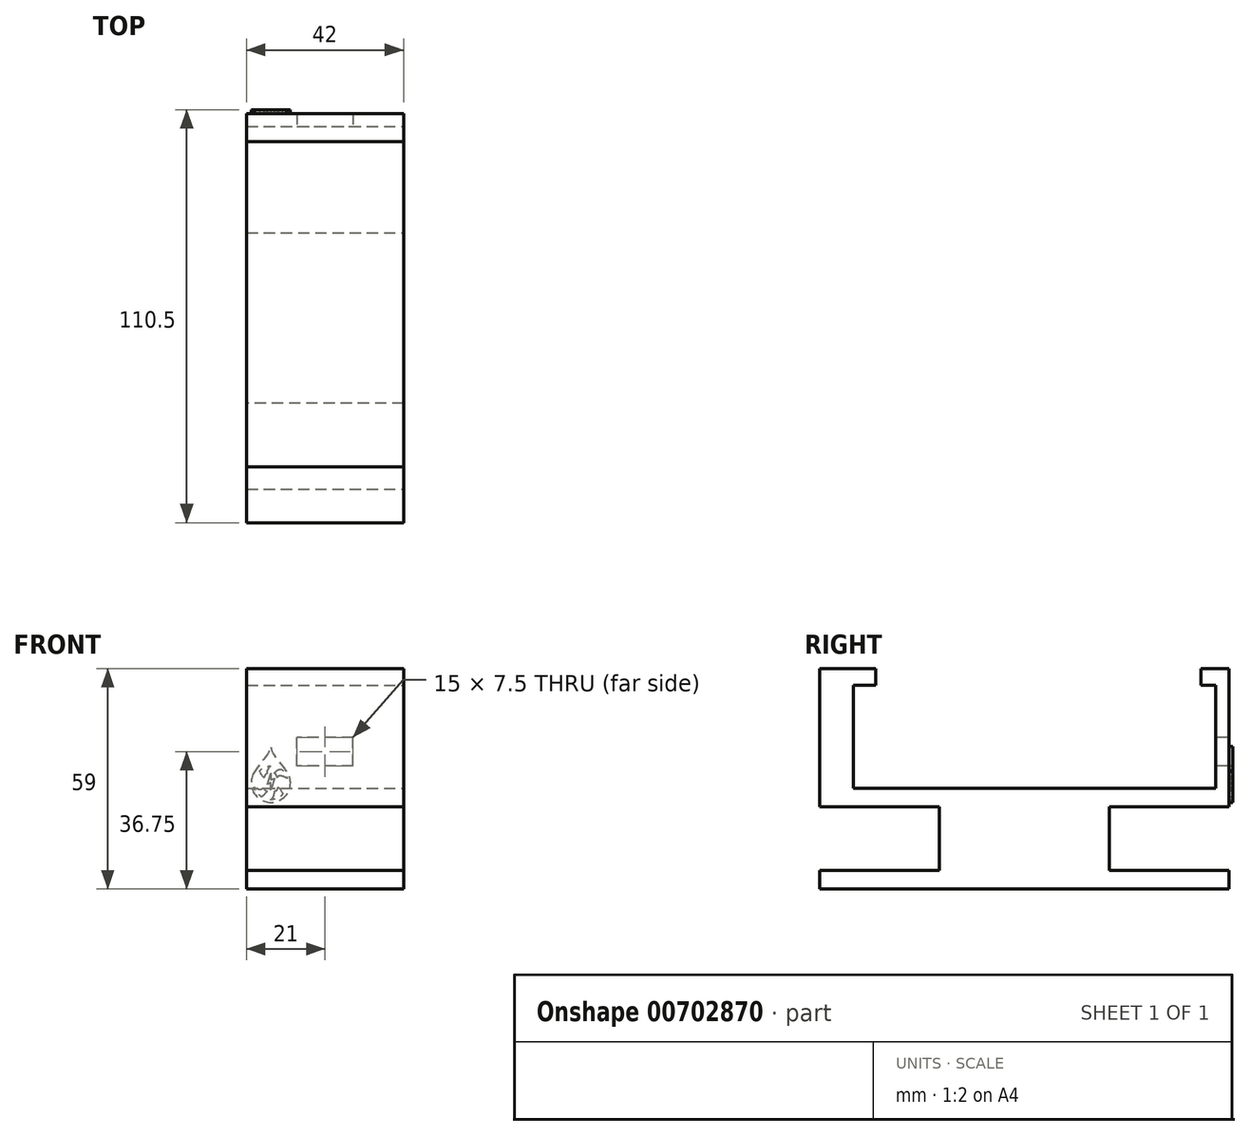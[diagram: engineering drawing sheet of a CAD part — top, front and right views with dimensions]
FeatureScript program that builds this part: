
annotation { "Feature Type Name" : "Feature", "Feature Type Description" : "" }
export const myFeature = defineFeature(function(context is Context, id is Id, definition is map)
    precondition{}
    {
        {
            var Q0;
            Q0=qCreatedBy(makeId("Top.planeOp"),FACE);
            var sketch = newSketch(context, id + "F0", { "sketchPlane" : qUnion([Q0])});
            skLineSegment(sketch, "E0.bottom", {"start": v(-21, 54.75) * mm, "end": v(21, 54.75) * mm});
            skLineSegment(sketch, "E0.top", {"start": v(-21, -54.75) * mm, "end": v(21, -54.75) * mm});
            skLineSegment(sketch, "E0.left", {"start": v(-21, 54.75) * mm, "end": v(-21, -54.75) * mm});
            skLineSegment(sketch, "E0.right", {"start": v(21, 54.75) * mm, "end": v(21, -54.75) * mm});
            skPoint(sketch, "E0.middle", {"position": v(0, 0) * mm});
            skSolve(sketch);
        }
        {
            var Q0;
            Q0=makeQuery(id+"F0.imprint","IMPRINT",FACE,{"disambiguationData":[TD([[makeQuery(id+"F0.imprint","IMPRINT",EDGE,{"derivedFrom":sQuery(id+"F0.wireOp",EDGE,"E0.bottom")}),-1.0]])]});
            extrude(context, id + "F1", {"entities" : qUnion([Q0]), "depth" : 5 * mm, "offsetDistance" : 25 * mm});
        }
        {
            var Q0;
            Q0=makeQuery(id+"F1.opExtrude","CAP_FACE",FACE,{"disambiguationData":[OSD([sQuery(id+"F0.wireOp",EDGE,"E0.bottom"),sQuery(id+"F0.wireOp",EDGE,"E0.top"),sQuery(id+"F0.wireOp",EDGE,"E0.left"),sQuery(id+"F0.wireOp",EDGE,"E0.right")])],"isStart":false});
            var sketch = newSketch(context, id + "F2", { "sketchPlane" : qUnion([Q0])});
            skLineSegment(sketch, "E1.bottom", {"start": v(-21, 54.75) * mm, "end": v(21, 54.75) * mm});
            skLineSegment(sketch, "E1.top", {"start": v(-21, 47.25) * mm, "end": v(21, 47.25) * mm});
            skLineSegment(sketch, "E1.left", {"start": v(-21, 54.75) * mm, "end": v(-21, 47.25) * mm});
            skLineSegment(sketch, "E1.right", {"start": v(21, 54.75) * mm, "end": v(21, 47.25) * mm});
            skPoint(sketch, "E1.middle", {"position": v(0, 51) * mm});
            skLineSegment(sketch, "E2.bottom", {"start": v(-21, -39.75) * mm, "end": v(21, -39.75) * mm});
            skLineSegment(sketch, "E2.top", {"start": v(-21, -54.75) * mm, "end": v(21, -54.75) * mm});
            skLineSegment(sketch, "E2.left", {"start": v(-21, -39.75) * mm, "end": v(-21, -54.75) * mm});
            skLineSegment(sketch, "E2.right", {"start": v(21, -39.75) * mm, "end": v(21, -54.75) * mm});
            skPoint(sketch, "E2.middle", {"position": v(0, -47.25) * mm});
            skSolve(sketch);
        }
        {
            var Q0;
            Q0=makeQuery(id+"F2.imprint","IMPRINT",FACE,{"disambiguationData":[TD([[makeQuery(id+"F2.imprint","IMPRINT",EDGE,{"derivedFrom":sQuery(id+"F2.wireOp",EDGE,"gTRGSuqZ-lPxv-xSsv-gjWA-rCe4dbmy2frY.bottom")}),-1.0]])]});
            var Q1;
            Q1=makeQuery(id+"F2.imprint","IMPRINT",FACE,{"disambiguationData":[TD([[makeQuery(id+"F2.imprint","IMPRINT",EDGE,{"derivedFrom":sQuery(id+"F2.wireOp",EDGE,"5NfKlNX9-xNwy-tjNF-5iGd-XRvzVmTsgCSR.bottom")}),1.0]])]});
            var Q2;
            Q2=makeQuery(id+"F2.imprint","IMPRINT",FACE,{"disambiguationData":[TD([[makeQuery(id+"F2.imprint","IMPRINT",EDGE,{"derivedFrom":sQuery(id+"F2.wireOp",EDGE,"E1.bottom")}),-1.0]])]});
            var Q3;
            Q3=makeQuery(id+"F2.imprint","IMPRINT",FACE,{"disambiguationData":[TD([[makeQuery(id+"F2.imprint","IMPRINT",EDGE,{"derivedFrom":sQuery(id+"F2.wireOp",EDGE,"E2.bottom")}),-1.0]])]});
            extrude(context, id + "F3", {"entities" : qUnion([Q0, Q1, Q2, Q3]), "operationType" : NewBodyOperationType.ADD, "depth" : 32 * mm, "offsetDistance" : 25 * mm});
        }
        {
            var Q0;
            Q0=makeQuery(id+"F3.opExtrude","SWEPT_FACE",FACE,{"disambiguationData":[OSD([sQuery(id+"F2.wireOp",EDGE,"E1.top")])]});
            var sketch = newSketch(context, id + "F4", { "sketchPlane" : qUnion([Q0])});
            skLineSegment(sketch, "E3.bottom", {"start": v(-21, 32.5) * mm, "end": v(21, 32.5) * mm});
            skLineSegment(sketch, "E3.top", {"start": v(-21, 5) * mm, "end": v(21, 5) * mm});
            skLineSegment(sketch, "E3.left", {"start": v(-21, 32.5) * mm, "end": v(-21, 5) * mm});
            skLineSegment(sketch, "E3.right", {"start": v(21, 32.5) * mm, "end": v(21, 5) * mm});
            skSolve(sketch);
        }
        {
            var Q0;
            Q0=makeQuery(id+"F4.imprint","IMPRINT",FACE,{"disambiguationData":[TD([[makeQuery(id+"F4.imprint","IMPRINT",EDGE,{"derivedFrom":sQuery(id+"F4.wireOp",EDGE,"E3.bottom")}),-1.0]])]});
            extrude(context, id + "F5", {"entities" : qUnion([Q0]), "operationType" : NewBodyOperationType.REMOVE, "oppositeDirection" : true, "depth" : 4 * mm, "offsetDistance" : 25 * mm});
        }
        {
            var Q0;
            Q0=makeQuery(id+"F3.opExtrude","SWEPT_FACE",FACE,{"disambiguationData":[OSD([sQuery(id+"F2.wireOp",EDGE,"E2.bottom")])]});
            var sketch = newSketch(context, id + "F6", { "sketchPlane" : qUnion([Q0])});
            skLineSegment(sketch, "E4.bottom", {"start": v(-21, 32.5) * mm, "end": v(21, 32.5) * mm});
            skLineSegment(sketch, "E4.top", {"start": v(-21, 5) * mm, "end": v(21, 5) * mm});
            skLineSegment(sketch, "E4.left", {"start": v(-21, 32.5) * mm, "end": v(-21, 5) * mm});
            skLineSegment(sketch, "E4.right", {"start": v(21, 32.5) * mm, "end": v(21, 5) * mm});
            skSolve(sketch);
        }
        {
            var Q0;
            Q0=makeQuery(id+"F6.imprint","IMPRINT",FACE,{"disambiguationData":[TD([[makeQuery(id+"F6.imprint","IMPRINT",EDGE,{"derivedFrom":sQuery(id+"F6.wireOp",EDGE,"E4.bottom")}),-1.0]])]});
            extrude(context, id + "F7", {"entities" : qUnion([Q0]), "operationType" : NewBodyOperationType.REMOVE, "oppositeDirection" : true, "depth" : 6 * mm, "offsetDistance" : 25 * mm});
        }
        {
            var Q0;
            Q0=makeQuery(id+"F5.boolean.opBoolean","COPY",FACE,{"derivedFrom":makeQuery(id+"F5.opExtrude","CAP_FACE",FACE,{"disambiguationData":[OSD([sQuery(id+"F4.wireOp",EDGE,"E3.bottom"),sQuery(id+"F4.wireOp",EDGE,"E3.top"),sQuery(id+"F4.wireOp",EDGE,"E3.left"),sQuery(id+"F4.wireOp",EDGE,"E3.right")])],"isStart":false})});
            var sketch = newSketch(context, id + "F8", { "sketchPlane" : qUnion([Q0])});
            skLineSegment(sketch, "E5.bottom", {"start": v(-7.5, 18.5) * mm, "end": v(7.5, 18.5) * mm});
            skLineSegment(sketch, "E5.top", {"start": v(-7.5, 11) * mm, "end": v(7.5, 11) * mm});
            skLineSegment(sketch, "E5.left", {"start": v(-7.5, 18.5) * mm, "end": v(-7.5, 11) * mm});
            skLineSegment(sketch, "E5.right", {"start": v(7.5, 18.5) * mm, "end": v(7.5, 11) * mm});
            skPoint(sketch, "E5.middle", {"position": v(0, 14.75) * mm});
            skSolve(sketch);
        }
        {
            var Q0;
            Q0=makeQuery(id+"F8.imprint","IMPRINT",FACE,{"disambiguationData":[TD([[makeQuery(id+"F8.imprint","IMPRINT",EDGE,{"derivedFrom":sQuery(id+"F8.wireOp",EDGE,"E5.bottom")}),-1.0]])]});
            extrude(context, id + "F9", {"entities" : qUnion([Q0]), "operationType" : NewBodyOperationType.REMOVE, "endBound" : BoundingType.THROUGH_ALL, "oppositeDirection" : true, "depth" : 25 * mm, "offsetDistance" : 25 * mm});
        }
        {
            var Q0;
            Q0=makeQuery(id+"F1.opExtrude","CAP_FACE",FACE,{"disambiguationData":[OSD([sQuery(id+"F0.wireOp",EDGE,"E0.bottom"),sQuery(id+"F0.wireOp",EDGE,"E0.top"),sQuery(id+"F0.wireOp",EDGE,"E0.left"),sQuery(id+"F0.wireOp",EDGE,"E0.right")])],"isStart":true});
            var sketch = newSketch(context, id + "F10", { "sketchPlane" : qUnion([Q0])});
            skLineSegment(sketch, "E6.bottom", {"start": v(-21, -54.75) * mm, "end": v(21, -54.75) * mm});
            skLineSegment(sketch, "E6.top", {"start": v(-21, 0) * mm, "end": v(21, 0) * mm});
            skLineSegment(sketch, "E6.left", {"start": v(-21, -54.75) * mm, "end": v(-21, 0) * mm});
            skLineSegment(sketch, "E6.right", {"start": v(21, -54.75) * mm, "end": v(21, 0) * mm});
            skLineSegment(sketch, "E7.bottom", {"start": v(-21, 54.75) * mm, "end": v(21, 54.75) * mm});
            skLineSegment(sketch, "E7.left", {"start": v(-21, 54.75) * mm, "end": v(-21, 0) * mm});
            skLineSegment(sketch, "E7.right", {"start": v(21, 54.75) * mm, "end": v(21, 0) * mm});
            skSolve(sketch);
        }
        {
            var Q0;
            Q0 = qSketchRegion(id + "F10", true);
            extrude(context, id + "F11", {"entities" : qUnion([Q0]), "operationType" : NewBodyOperationType.ADD, "depth" : 22 * mm, "offsetDistance" : 25 * mm});
        }
        {
            var Q0;
            Q0=makeQuery(id+"F11.boolean.opBoolean","MERGE",FACE,{"derivedFrom":[makeQuery(id+"F3.boolean.opBoolean","MERGE",FACE,{"derivedFrom":[makeQuery(id+"F1.opExtrude","SWEPT_FACE",FACE,{"disambiguationData":[OSD([sQuery(id+"F0.wireOp",EDGE,"E0.bottom")])]}),makeQuery(id+"F3.opExtrude","SWEPT_FACE",FACE,{"disambiguationData":[OSD([sQuery(id+"F2.wireOp",EDGE,"E1.bottom")])]})]}),makeQuery(id+"F11.opExtrude","SWEPT_FACE",FACE,{"disambiguationData":[OSD([sQuery(id+"F10.wireOp",EDGE,"E6.bottom")])]})]});
            var sketch = newSketch(context, id + "F12", { "sketchPlane" : qUnion([Q0])});
            skLineSegment(sketch, "E8.bottom", {"start": v(21, -17) * mm, "end": v(-21, -17) * mm});
            skLineSegment(sketch, "E8.top", {"start": v(21, 0) * mm, "end": v(-21, 0) * mm});
            skLineSegment(sketch, "E8.left", {"start": v(21, -17) * mm, "end": v(21, 0) * mm});
            skLineSegment(sketch, "E8.right", {"start": v(-21, -17) * mm, "end": v(-21, 0) * mm});
            skSolve(sketch);
        }
        {
            var Q0;
            Q0=makeQuery(id+"F12.imprint","IMPRINT",FACE,{"disambiguationData":[TD([[makeQuery(id+"F12.imprint","IMPRINT",EDGE,{"derivedFrom":sQuery(id+"F12.wireOp",EDGE,"E8.bottom")}),-1.0]])]});
            extrude(context, id + "F13", {"entities" : qUnion([Q0]), "operationType" : NewBodyOperationType.REMOVE, "oppositeDirection" : true, "depth" : 32 * mm, "offsetDistance" : 25 * mm});
        }
        {
            var Q0;
            Q0=makeQuery(id+"F11.boolean.opBoolean","MERGE",FACE,{"derivedFrom":[makeQuery(id+"F3.boolean.opBoolean","MERGE",FACE,{"derivedFrom":[makeQuery(id+"F1.opExtrude","SWEPT_FACE",FACE,{"disambiguationData":[OSD([sQuery(id+"F0.wireOp",EDGE,"E0.top")])]}),makeQuery(id+"F3.opExtrude","SWEPT_FACE",FACE,{"disambiguationData":[OSD([sQuery(id+"F2.wireOp",EDGE,"E2.top")])]})]}),makeQuery(id+"F11.opExtrude","SWEPT_FACE",FACE,{"disambiguationData":[OSD([sQuery(id+"F10.wireOp",EDGE,"E7.bottom")])]})]});
            var sketch = newSketch(context, id + "F14", { "sketchPlane" : qUnion([Q0])});
            skLineSegment(sketch, "E9.bottom", {"start": v(21, -17) * mm, "end": v(-21, -17) * mm});
            skLineSegment(sketch, "E9.top", {"start": v(21, 0) * mm, "end": v(-21, 0) * mm});
            skLineSegment(sketch, "E9.left", {"start": v(21, -17) * mm, "end": v(21, 0) * mm});
            skLineSegment(sketch, "E9.right", {"start": v(-21, -17) * mm, "end": v(-21, 0) * mm});
            skSolve(sketch);
        }
        {
            var Q0;
            Q0=makeQuery(id+"F14.imprint","IMPRINT",FACE,{"disambiguationData":[TD([[makeQuery(id+"F14.imprint","IMPRINT",EDGE,{"derivedFrom":sQuery(id+"F14.wireOp",EDGE,"E9.bottom")}),-1.0]])]});
            extrude(context, id + "F15", {"entities" : qUnion([Q0]), "operationType" : NewBodyOperationType.REMOVE, "oppositeDirection" : true, "depth" : 32 * mm, "offsetDistance" : 25 * mm});
        }
        {
            var Q0;
            {var subQ2=sQuery(id+"F2.wireOp",EDGE,"E1.bottom");Q0=makeQuery(id+"F13.boolean.opBoolean","SPLIT",FACE,{"disambiguationData":[TD([makeQuery(id+"F9.boolean.opBoolean","COPY",FACE,{"derivedFrom":makeQuery(id+"F9.opExtrude","SWEPT_FACE",FACE,{"disambiguationData":[OSD([sQuery(id+"F8.wireOp",EDGE,"E5.bottom")])]})})])],"derivedFrom":makeQuery(id+"F11.boolean.opBoolean","MERGE",FACE,{"derivedFrom":[makeQuery(id+"F3.boolean.opBoolean","MERGE",FACE,{"derivedFrom":[makeQuery(id+"F1.opExtrude","SWEPT_FACE",FACE,{"disambiguationData":[OSD([sQuery(id+"F0.wireOp",EDGE,"E0.bottom")])]}),makeQuery(id+"F3.opExtrude","SWEPT_FACE",FACE,{"disambiguationData":[OSD([subQ2])]})]}),makeQuery(id+"F11.opExtrude","SWEPT_FACE",FACE,{"disambiguationData":[OSD([sQuery(id+"F10.wireOp",EDGE,"E6.bottom")])]})]})});}
            var sketch = newSketch(context, id + "F16", { "sketchPlane" : qUnion([Q0])});
            skCircle(sketch, "E10", {"center": v(14.5, 6.44) * mm, "radius": 5.26 * mm});
            skFitSpline(sketch, "E11", {"points": [v(9.9, 9) * mm, v(13.99, 14.6) * mm, v(14.56, 16.18) * mm, v(15.14, 14.6) * mm, v(18.8, 9.46) * mm], "startDerivative": vector(16.98, 26.88) * mm, "endDerivative": vector(16.85, -27.07) * mm});
            skLineSegment(sketch, "E12", {"start": v(14.5, 7.28) * mm, "end": v(13.47, 7.64) * mm});
            skLineSegment(sketch, "E13", {"start": v(13.47, 7.64) * mm, "end": v(14.5, 4.52) * mm});
            skLineSegment(sketch, "E14", {"start": v(14.5, 4.52) * mm, "end": v(14.5, 6.44) * mm});
            skLineSegment(sketch, "E15", {"start": v(14.5, 6.44) * mm, "end": v(15.39, 6) * mm});
            skLineSegment(sketch, "E16", {"start": v(15.39, 6) * mm, "end": v(14.5, 9.02) * mm});
            skLineSegment(sketch, "E17", {"start": v(14.5, 9.02) * mm, "end": v(14.5, 7.28) * mm});
            skFitSpline(sketch, "E18", {"points": [v(16.34, 7.72) * mm, v(17.24, 9.89) * mm, v(14.5, 10.94) * mm], "startDerivative": vector(5.76, 7.92) * mm, "endDerivative": vector(-5.08, -0.17) * mm});
            skFitSpline(sketch, "E19", {"points": [v(14.5, 10.94) * mm, v(15.4, 9.02) * mm], "startDerivative": vector(2.42, -1.84) * mm, "endDerivative": vector(-1.27, -0.47) * mm});
            skFitSpline(sketch, "E20", {"points": [v(13.59, 9.02) * mm, v(11.74, 10.05) * mm, v(10.1, 7.6) * mm], "startDerivative": vector(-3.42, 3.64) * mm, "endDerivative": vector(-2.44, -5.45) * mm});
            skFitSpline(sketch, "E21", {"points": [v(10.1, 7.6) * mm, v(12.74, 7.6) * mm], "startDerivative": vector(2.22, 1.16) * mm, "endDerivative": vector(0, -4.31) * mm});
            skFitSpline(sketch, "E22", {"points": [v(15.4, 9.02) * mm, v(16.34, 7.72) * mm], "startDerivative": vector(1.63, -0.68) * mm, "endDerivative": vector(0.65, -1.86) * mm});
            skFitSpline(sketch, "E23", {"points": [v(12.73, 7.73) * mm, v(13.59, 9.02) * mm], "startDerivative": vector(0.63, 2.17) * mm, "endDerivative": vector(1.3, 0.45) * mm});
            skFitSpline(sketch, "E24", {"points": [v(12.51, 5.25) * mm, v(11.53, 3.12) * mm, v(14.56, 1.84) * mm], "startDerivative": vector(-6.57, -6.68) * mm, "endDerivative": vector(5.86, -1.17) * mm});
            skFitSpline(sketch, "E25", {"points": [v(14.56, 1.84) * mm, v(13.57, 4.24) * mm], "startDerivative": vector(-0.1, 0.44) * mm, "endDerivative": vector(0.66, 4.7) * mm});
            skFitSpline(sketch, "E26", {"points": [v(13.57, 4.24) * mm, v(12.51, 5.25) * mm], "startDerivative": vector(-2.26, 0.13) * mm, "endDerivative": vector(-0.52, 1.5) * mm});
            skFitSpline(sketch, "E27", {"points": [v(15.42, 4.18) * mm, v(17.1, 2.77) * mm, v(19.04, 5.25) * mm], "startDerivative": vector(7.14, -6.76) * mm, "endDerivative": vector(2.64, 5.36) * mm});
            skFitSpline(sketch, "E28", {"points": [v(19.04, 5.25) * mm, v(16.47, 5.14) * mm], "startDerivative": vector(-2.16, -0.83) * mm, "endDerivative": vector(-2.61, 2.84) * mm});
            skFitSpline(sketch, "E29", {"points": [v(16.47, 5.14) * mm, v(15.42, 4.18) * mm], "startDerivative": vector(-0.71, -2.15) * mm, "endDerivative": vector(-1.3, -0.4) * mm});
            skSolve(sketch);
        }
        {
            var Q0;
            Q0 = qSketchRegion(id + "F16", true);
            extrude(context, id + "F17", {"entities" : qUnion([Q0]), "operationType" : NewBodyOperationType.ADD, "depth" : 1 * mm, "offsetDistance" : 25 * mm});
        }
    });
